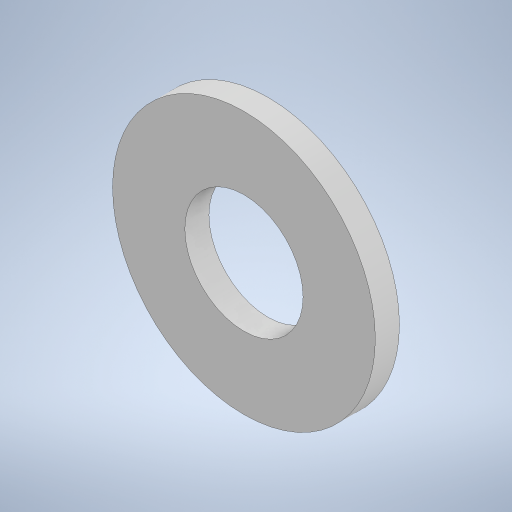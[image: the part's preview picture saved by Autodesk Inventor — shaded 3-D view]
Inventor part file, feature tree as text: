
AUTODESK INVENTOR PART (.ipt)
format: ipt  version: 2023 (Build 270158000, 158)  size: 219,648 bytes
history: native  units: in
note: dims shown in document units (in); Inventor stores cm internally (conversion verified against a paired STEP export)
features: extrude x1, sketch x1
ambient origin geometry x8: Origin, YZ Plane, XZ Plane, XY Plane, X Axis, Y Axis, Z Axis, Center Point
bodies: Solid1 (feature_tree)
feature tree (2):
  extrude  "Extrusion1"  Depth=0.0217in
  sketch  "Sketch1"  dims[d0=0.1063in d1=0.2362in d2=0.0217in d3=0.0in d4=0.0in d5=0.0in d6=0.0in d7=0.0in]
